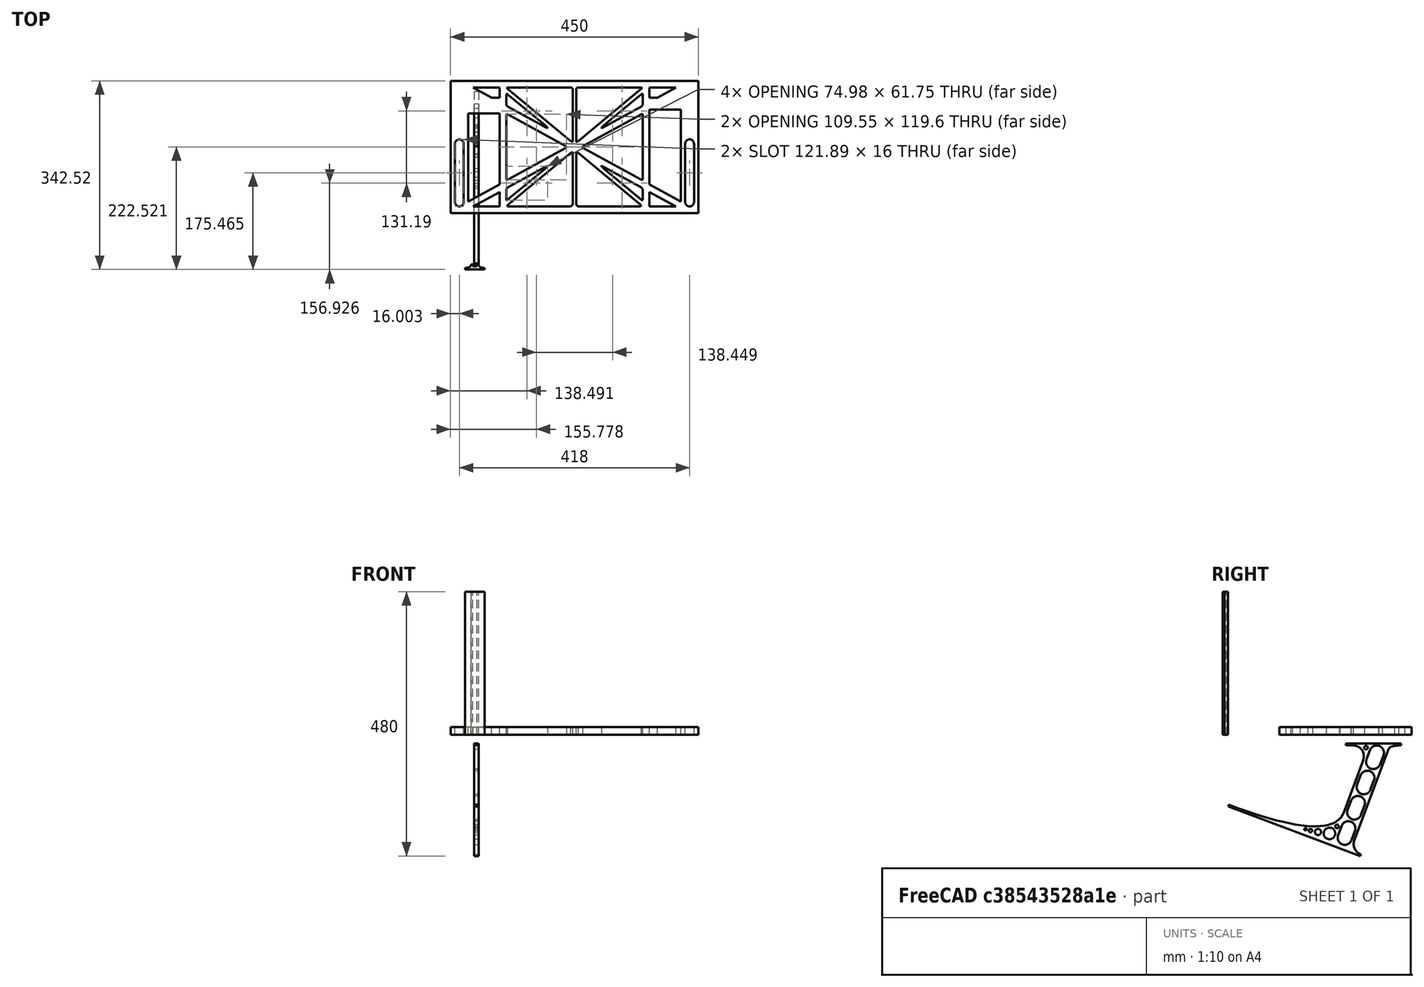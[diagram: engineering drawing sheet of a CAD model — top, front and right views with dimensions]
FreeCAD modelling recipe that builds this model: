
FCSTD DOCUMENT  (FreeCAD 0.19R0.19.2)
Label: laptopStand095
License: All rights reserved
LicenseURL: http://en.wikipedia.org/wiki/All_rights_reserved
objects: Sketcher::SketchObject×3, Part::Extrusion×3
note: 6 computed .brp shape members not serialized (recipe doc carries the construction recipe); baked Part::Feature solids carry a one-line shape summary decoded from their .brp

FEATURE [Sketcher::SketchObject] Sketch
  FullyConstrained = false
  sketch-geometry (252):
    g0: LineSegment StartX=-10.9272 StartY=-82.7794 StartZ=0 EndX=46.0728 EndY=-51.4823 EndZ=0
    g1: LineSegment StartX=366.073 StartY=-91.7794 StartZ=0 EndX=318.073 EndY=-65.424 EndZ=0
    g2: LineSegment StartX=-10.9272 StartY=77.3346 StartZ=0 EndX=-10.9272 EndY=-82.7794 EndZ=0
    g3: LineSegment StartX=375.073 StartY=-82.7794 StartZ=0 EndX=375.073 EndY=83.9235 EndZ=0
    g4: LineSegment StartX=-1.92719 StartY=-91.7794 StartZ=0 EndX=46.0728 EndY=-91.7794 EndZ=0
    g5: LineSegment StartX=318.073 StartY=124.221 StartZ=0 EndX=366.073 EndY=124.221 EndZ=0
    g6: LineSegment StartX=318.073 StartY=83.9235 StartZ=0 EndX=318.073 EndY=-51.4823 EndZ=0
    g7: LineSegment StartX=318.073 StartY=-51.4823 StartZ=0 EndX=375.073 EndY=-82.7794 EndZ=0
    g8: LineSegment StartX=318.073 StartY=-65.424 StartZ=0 EndX=318.073 EndY=-91.7794 EndZ=0
    g9: LineSegment StartX=318.073 StartY=-91.7794 StartZ=0 EndX=366.073 EndY=-91.7794 EndZ=0
    g10: LineSegment StartX=46.0728 StartY=-65.424 StartZ=0 EndX=-1.92719 EndY=-91.7794 EndZ=0
    g11: LineSegment StartX=46.0728 StartY=-65.424 StartZ=0 EndX=46.0728 EndY=-91.7794 EndZ=0
    g12: LineSegment StartX=46.0728 StartY=77.3346 StartZ=0 EndX=46.0728 EndY=-51.4823 EndZ=0
    g13: LineSegment StartX=-42.9272 StartY=136.221 StartZ=0 EndX=-42.9272 EndY=-103.779 EndZ=0
    g14: LineSegment StartX=407.073 StartY=136.221 StartZ=0 EndX=407.073 EndY=-103.779 EndZ=0
    g15: ArcOfCircle CenterX=-26.9272 CenterY=22.1087 CenterZ=0 NormalX=0 NormalY=0 NormalZ=1 AngleXU=0 Radius=8 StartAngle=1e-16 EndAngle=3.14159
    g16: ArcOfCircle CenterX=-26.9272 CenterY=-83.7794 CenterZ=0 NormalX=0 NormalY=0 NormalZ=1 AngleXU=0 Radius=8 StartAngle=3.14159 EndAngle=6.28319
    g17: LineSegment StartX=-34.9272 StartY=22.1087 StartZ=0 EndX=-34.9272 EndY=-83.7794 EndZ=0
    g18: LineSegment StartX=-18.9272 StartY=22.1087 StartZ=0 EndX=-18.9272 EndY=-83.7794 EndZ=0
    g19: ArcOfCircle CenterX=391.073 CenterY=22.1087 CenterZ=0 NormalX=0 NormalY=0 NormalZ=1 AngleXU=0 Radius=8 StartAngle=-4.4e-15 EndAngle=3.14159
    g20: LineSegment StartX=399.073 StartY=22.1087 StartZ=0 EndX=399.073 EndY=-83.7794 EndZ=0
    g21: LineSegment StartX=383.073 StartY=22.1087 StartZ=0 EndX=383.073 EndY=-83.7794 EndZ=0
    g22: ArcOfCircle CenterX=391.073 CenterY=-83.7794 CenterZ=0 NormalX=0 NormalY=0 NormalZ=1 AngleXU=0 Radius=8 StartAngle=3.14159 EndAngle=6.28319
    g23: Circle CenterX=175.022 CenterY=27.0628 CenterZ=0 NormalX=0 NormalY=0 NormalZ=1 AngleXU=0 Radius=1
    g24: Circle CenterX=179.022 CenterY=24.8665 CenterZ=0 NormalX=0 NormalY=0 NormalZ=1 AngleXU=0 Radius=1
    g25: Circle CenterX=179.022 CenterY=27.0628 CenterZ=0 NormalX=0 NormalY=0 NormalZ=1 AngleXU=0 Radius=1
    g26: BSplineCurve PolesCount=3 KnotsCount=2 Degree=2 IsPeriodic=0
    g27: GeomPoint X=175.022 Y=27.0628 Z=0
    g28: GeomPoint X=179.022 Y=27.0628 Z=0
    g29: Circle CenterX=189.124 CenterY=27.0628 CenterZ=0 NormalX=0 NormalY=0 NormalZ=1 AngleXU=0 Radius=1
    g30: Circle CenterX=185.124 CenterY=24.8665 CenterZ=0 NormalX=0 NormalY=0 NormalZ=1 AngleXU=0 Radius=1
    g31: Circle CenterX=185.124 CenterY=27.0628 CenterZ=0 NormalX=0 NormalY=0 NormalZ=1 AngleXU=0 Radius=1
    g32: BSplineCurve PolesCount=3 KnotsCount=2 Degree=2 IsPeriodic=0
    g33: GeomPoint X=189.124 Y=27.0628 Z=0
    g34: GeomPoint X=185.124 Y=27.0628 Z=0
    g35: Circle CenterX=175.022 CenterY=5.37834 CenterZ=0 NormalX=0 NormalY=0 NormalZ=1 AngleXU=0 Radius=1
    g36: Circle CenterX=179.022 CenterY=7.57463 CenterZ=0 NormalX=0 NormalY=0 NormalZ=1 AngleXU=0 Radius=1
    g37: Circle CenterX=179.022 CenterY=5.34704 CenterZ=0 NormalX=0 NormalY=0 NormalZ=1 AngleXU=0 Radius=1
    g38: BSplineCurve PolesCount=3 KnotsCount=2 Degree=2 IsPeriodic=0
    g39: GeomPoint X=175.022 Y=5.37834 Z=0
    g40: GeomPoint X=179.022 Y=5.34704 Z=0
    g41: Circle CenterX=189.124 CenterY=5.37834 CenterZ=0 NormalX=0 NormalY=0 NormalZ=1 AngleXU=0 Radius=1
    g42: Circle CenterX=185.124 CenterY=7.57463 CenterZ=0 NormalX=0 NormalY=0 NormalZ=1 AngleXU=0 Radius=1
    g43: Circle CenterX=185.124 CenterY=5.34704 CenterZ=0 NormalX=0 NormalY=0 NormalZ=1 AngleXU=0 Radius=1
    g44: BSplineCurve PolesCount=3 KnotsCount=2 Degree=2 IsPeriodic=0
    g45: GeomPoint X=189.124 Y=5.37834 Z=0
    g46: GeomPoint X=185.124 Y=5.34704 Z=0
    g47: Circle CenterX=165.871 CenterY=18.1458 CenterZ=0 NormalX=0 NormalY=0 NormalZ=1 AngleXU=0 Radius=1
    g48: Circle CenterX=169.377 CenterY=16.2206 CenterZ=0 NormalX=0 NormalY=0 NormalZ=1 AngleXU=0 Radius=1
    g49: Circle CenterX=165.871 CenterY=14.2954 CenterZ=0 NormalX=0 NormalY=0 NormalZ=1 AngleXU=0 Radius=1
    g50: BSplineCurve PolesCount=3 KnotsCount=2 Degree=2 IsPeriodic=0
    g51: GeomPoint X=165.871 Y=18.1458 Z=0
    g52: GeomPoint X=165.871 Y=14.2954 Z=0
    g53: Circle CenterX=198.275 CenterY=18.1458 CenterZ=0 NormalX=0 NormalY=0 NormalZ=1 AngleXU=0 Radius=1
    g54: Circle CenterX=194.768 CenterY=16.2206 CenterZ=0 NormalX=0 NormalY=0 NormalZ=1 AngleXU=0 Radius=1
    g55: Circle CenterX=198.275 CenterY=14.2954 CenterZ=0 NormalX=0 NormalY=0 NormalZ=1 AngleXU=0 Radius=1
    g56: BSplineCurve PolesCount=3 KnotsCount=2 Degree=2 IsPeriodic=0
    g57: GeomPoint X=198.275 Y=18.1458 Z=0
    g58: GeomPoint X=198.275 Y=14.2954 Z=0
    g59: LineSegment StartX=407.073 StartY=-103.779 StartZ=0 EndX=-42.9272 EndY=-103.779 EndZ=0
    g60: LineSegment StartX=407.073 StartY=136.221 StartZ=0 EndX=-42.9272 EndY=136.221 EndZ=0
    g61: LineSegment StartX=46.0728 StartY=77.3346 StartZ=0 EndX=-10.9272 EndY=77.3346 EndZ=0
    g62: LineSegment StartX=46.0728 StartY=105.865 StartZ=0 EndX=31.5028 EndY=105.865 EndZ=0
    g63: LineSegment StartX=46.0728 StartY=124.221 StartZ=0 EndX=46.0728 EndY=105.865 EndZ=0
    g64: LineSegment StartX=-1.92719 StartY=124.221 StartZ=0 EndX=31.5028 EndY=105.865 EndZ=0
    g65: LineSegment StartX=46.0728 StartY=124.221 StartZ=0 EndX=-1.92719 EndY=124.221 EndZ=0
    g66: LineSegment StartX=318.073 StartY=83.9235 StartZ=0 EndX=375.073 EndY=83.9235 EndZ=0
    g67: Circle CenterX=125.607 CenterY=54.1951 CenterZ=0 NormalX=0 NormalY=0 NormalZ=1 AngleXU=0 Radius=1
    g68: Circle CenterX=139.632 CenterY=46.4944 CenterZ=0 NormalX=0 NormalY=0 NormalZ=1 AngleXU=0 Radius=1
    g69: Circle CenterX=127.326 CenterY=56.7187 CenterZ=0 NormalX=0 NormalY=0 NormalZ=1 AngleXU=0 Radius=1
    g70: BSplineCurve PolesCount=3 KnotsCount=2 Degree=2 IsPeriodic=0
    g71: GeomPoint X=125.607 Y=54.1951 Z=0
    g72: GeomPoint X=127.326 Y=56.7187 Z=0
    g73: Circle CenterX=236.821 CenterY=56.7187 CenterZ=0 NormalX=0 NormalY=0 NormalZ=1 AngleXU=0 Radius=1
    g74: Circle CenterX=224.513 CenterY=46.4944 CenterZ=0 NormalX=0 NormalY=0 NormalZ=1 AngleXU=0 Radius=1
    g75: Circle CenterX=238.538 CenterY=54.1951 CenterZ=0 NormalX=0 NormalY=0 NormalZ=1 AngleXU=0 Radius=1
    g76: BSplineCurve PolesCount=3 KnotsCount=2 Degree=2 IsPeriodic=0
    g77: GeomPoint X=236.821 Y=56.7187 Z=0
    g78: GeomPoint X=238.538 Y=54.1951 Z=0
    g79: Circle CenterX=238.538 CenterY=-21.7539 CenterZ=0 NormalX=0 NormalY=0 NormalZ=1 AngleXU=0 Radius=1
    g80: Circle CenterX=224.513 CenterY=-14.0532 CenterZ=0 NormalX=0 NormalY=0 NormalZ=1 AngleXU=0 Radius=1
    g81: Circle CenterX=236.821 CenterY=-24.2775 CenterZ=0 NormalX=0 NormalY=0 NormalZ=1 AngleXU=0 Radius=1
    g82: BSplineCurve PolesCount=3 KnotsCount=2 Degree=2 IsPeriodic=0
    g83: GeomPoint X=238.538 Y=-21.7539 Z=0
    g84: GeomPoint X=236.821 Y=-24.2775 Z=0
    g85: Circle CenterX=125.607 CenterY=-21.7539 CenterZ=0 NormalX=0 NormalY=0 NormalZ=1 AngleXU=0 Radius=1
    g86: Circle CenterX=139.632 CenterY=-14.0532 CenterZ=0 NormalX=0 NormalY=0 NormalZ=1 AngleXU=0 Radius=1
    g87: Circle CenterX=127.325 CenterY=-24.2775 CenterZ=0 NormalX=0 NormalY=0 NormalZ=1 AngleXU=0 Radius=1
    g88: BSplineCurve PolesCount=3 KnotsCount=2 Degree=2 IsPeriodic=0
    g89: GeomPoint X=125.607 Y=-21.7539 Z=0
    g90: GeomPoint X=127.325 Y=-24.2775 Z=0
    g91: Circle CenterX=302.996 CenterY=111.695 CenterZ=0 NormalX=0 NormalY=0 NormalZ=1 AngleXU=0 Radius=1
    g92: Circle CenterX=306.073 CenterY=114.251 CenterZ=0 NormalX=0 NormalY=0 NormalZ=1 AngleXU=0 Radius=1
    g93: Circle CenterX=306.073 CenterY=110.251 CenterZ=0 NormalX=0 NormalY=0 NormalZ=1 AngleXU=0 Radius=1
    g94: BSplineCurve PolesCount=3 KnotsCount=2 Degree=2 IsPeriodic=0
    g95: GeomPoint X=302.996 Y=111.695 Z=0
    g96: GeomPoint X=306.073 Y=110.251 Z=0
    g97: Circle CenterX=306.073 CenterY=95.2763 CenterZ=0 NormalX=0 NormalY=0 NormalZ=1 AngleXU=0 Radius=1
    g98: Circle CenterX=306.073 CenterY=91.2763 CenterZ=0 NormalX=0 NormalY=0 NormalZ=1 AngleXU=0 Radius=1
    g99: Circle CenterX=302.567 CenterY=89.3511 CenterZ=0 NormalX=0 NormalY=0 NormalZ=1 AngleXU=0 Radius=1
    g100: BSplineCurve PolesCount=3 KnotsCount=2 Degree=2 IsPeriodic=0
    g101: GeomPoint X=306.073 Y=95.2763 Z=0
    g102: GeomPoint X=302.567 Y=89.3511 Z=0
    g103: LineSegment StartX=306.073 StartY=110.251 StartZ=0 EndX=306.073 EndY=95.2763 EndZ=0
    g104: LineSegment StartX=302.996 StartY=111.695 StartZ=0 EndX=236.821 EndY=56.7187 EndZ=0
    g105: LineSegment StartX=238.538 StartY=54.1951 StartZ=0 EndX=302.567 EndY=89.3511 EndZ=0
    g106: Circle CenterX=61.1496 CenterY=111.695 CenterZ=0 NormalX=0 NormalY=0 NormalZ=1 AngleXU=0 Radius=1
    g107: Circle CenterX=58.0728 CenterY=114.251 CenterZ=0 NormalX=0 NormalY=0 NormalZ=1 AngleXU=0 Radius=1
    g108: Circle CenterX=58.0728 CenterY=110.251 CenterZ=0 NormalX=0 NormalY=0 NormalZ=1 AngleXU=0 Radius=1
    g109: BSplineCurve PolesCount=3 KnotsCount=2 Degree=2 IsPeriodic=0
    g110: GeomPoint X=61.1496 Y=111.695 Z=0
    g111: GeomPoint X=58.0728 Y=110.251 Z=0
    g112: Circle CenterX=61.5791 CenterY=89.3511 CenterZ=0 NormalX=0 NormalY=0 NormalZ=1 AngleXU=0 Radius=1
    g113: Circle CenterX=58.0728 CenterY=91.2763 CenterZ=0 NormalX=0 NormalY=0 NormalZ=1 AngleXU=0 Radius=1
    g114: Circle CenterX=58.0728 CenterY=95.2763 CenterZ=0 NormalX=0 NormalY=0 NormalZ=1 AngleXU=0 Radius=1
    g115: BSplineCurve PolesCount=3 KnotsCount=2 Degree=2 IsPeriodic=0
    g116: GeomPoint X=61.5791 Y=89.3511 Z=0
    g117: GeomPoint X=58.0728 Y=95.2763 Z=0
    g118: LineSegment StartX=58.0728 StartY=110.251 StartZ=0 EndX=58.0728 EndY=95.2763 EndZ=0
    g119: LineSegment StartX=61.1496 StartY=111.695 StartZ=0 EndX=127.326 EndY=56.7187 EndZ=0
    g120: LineSegment StartX=125.607 StartY=54.1951 StartZ=0 EndX=61.5791 EndY=89.3511 EndZ=0
    g121: Circle CenterX=61.5791 CenterY=-56.9099 CenterZ=0 NormalX=0 NormalY=0 NormalZ=1 AngleXU=0 Radius=1
    g122: Circle CenterX=58.0728 CenterY=-58.8351 CenterZ=0 NormalX=0 NormalY=0 NormalZ=1 AngleXU=0 Radius=1
    g123: Circle CenterX=58.0728 CenterY=-62.8351 CenterZ=0 NormalX=0 NormalY=0 NormalZ=1 AngleXU=0 Radius=1
    g124: BSplineCurve PolesCount=3 KnotsCount=2 Degree=2 IsPeriodic=0
    g125: GeomPoint X=61.5791 Y=-56.9099 Z=0
    g126: GeomPoint X=58.0728 Y=-62.8351 Z=0
    g127: Circle CenterX=58.0728 CenterY=-77.8102 CenterZ=0 NormalX=0 NormalY=0 NormalZ=1 AngleXU=0 Radius=1
    g128: Circle CenterX=58.0728 CenterY=-81.8102 CenterZ=0 NormalX=0 NormalY=0 NormalZ=1 AngleXU=0 Radius=1
    g129: Circle CenterX=61.1496 CenterY=-79.2541 CenterZ=0 NormalX=0 NormalY=0 NormalZ=1 AngleXU=0 Radius=1
    g130: BSplineCurve PolesCount=3 KnotsCount=2 Degree=2 IsPeriodic=0
    g131: GeomPoint X=58.0728 Y=-77.8102 Z=0
    g132: GeomPoint X=61.1496 Y=-79.2541 Z=0
    g133: LineSegment StartX=58.0728 StartY=-62.8351 StartZ=0 EndX=58.0728 EndY=-77.8102 EndZ=0
    g134: LineSegment StartX=61.1496 StartY=-79.2541 StartZ=0 EndX=127.325 EndY=-24.2775 EndZ=0
    g135: LineSegment StartX=125.607 StartY=-21.7539 StartZ=0 EndX=61.5791 EndY=-56.9099 EndZ=0
    g136: Circle CenterX=302.567 CenterY=-56.9099 CenterZ=0 NormalX=0 NormalY=0 NormalZ=1 AngleXU=0 Radius=1
    g137: Circle CenterX=306.073 CenterY=-58.8351 CenterZ=0 NormalX=0 NormalY=0 NormalZ=1 AngleXU=0 Radius=1
    g138: Circle CenterX=306.073 CenterY=-62.8351 CenterZ=0 NormalX=0 NormalY=0 NormalZ=1 AngleXU=0 Radius=1
    g139: BSplineCurve PolesCount=3 KnotsCount=2 Degree=2 IsPeriodic=0
    g140: GeomPoint X=302.567 Y=-56.9099 Z=0
    g141: GeomPoint X=306.073 Y=-62.8351 Z=0
    g142: Circle CenterX=302.996 CenterY=-79.2541 CenterZ=0 NormalX=0 NormalY=0 NormalZ=1 AngleXU=0 Radius=1
    g143: Circle CenterX=306.073 CenterY=-81.8102 CenterZ=0 NormalX=0 NormalY=0 NormalZ=1 AngleXU=0 Radius=1
    g144: Circle CenterX=306.073 CenterY=-77.8102 CenterZ=0 NormalX=0 NormalY=0 NormalZ=1 AngleXU=0 Radius=1
    g145: BSplineCurve PolesCount=3 KnotsCount=2 Degree=2 IsPeriodic=0
    g146: GeomPoint X=302.996 Y=-79.2541 Z=0
    g147: GeomPoint X=306.073 Y=-77.8102 Z=0
    g148: LineSegment StartX=306.073 StartY=-62.8351 StartZ=0 EndX=306.073 EndY=-77.8102 EndZ=0
    g149: LineSegment StartX=302.996 StartY=-79.2541 StartZ=0 EndX=236.821 EndY=-24.2775 EndZ=0
    g150: LineSegment StartX=238.538 StartY=-21.7539 StartZ=0 EndX=302.567 EndY=-56.9099 EndZ=0
    g151: Circle CenterX=61.6457 CenterY=-88.8112 CenterZ=0 NormalX=0 NormalY=0 NormalZ=1 AngleXU=0 Radius=1
    g152: Circle CenterX=58.0728 CenterY=-91.7794 CenterZ=0 NormalX=0 NormalY=0 NormalZ=1 AngleXU=0 Radius=1
    g153: Circle CenterX=63.9135 CenterY=-91.7794 CenterZ=0 NormalX=0 NormalY=0 NormalZ=1 AngleXU=0 Radius=1
    g154: BSplineCurve PolesCount=3 KnotsCount=2 Degree=2 IsPeriodic=0
    g155: GeomPoint X=61.6457 Y=-88.8112 Z=0
    g156: GeomPoint X=63.9135 Y=-91.7794 Z=0
    g157: Circle CenterX=179.022 CenterY=-85.8163 CenterZ=0 NormalX=0 NormalY=0 NormalZ=1 AngleXU=0 Radius=1
    g158: Circle CenterX=179.022 CenterY=-91.7794 CenterZ=0 NormalX=0 NormalY=0 NormalZ=1 AngleXU=0 Radius=1
    g159: Circle CenterX=171.895 CenterY=-91.7794 CenterZ=0 NormalX=0 NormalY=0 NormalZ=1 AngleXU=0 Radius=1
    g160: BSplineCurve PolesCount=3 KnotsCount=2 Degree=2 IsPeriodic=0
    g161: GeomPoint X=179.022 Y=-85.8163 Z=0
    g162: GeomPoint X=171.895 Y=-91.7794 Z=0
    g163: Circle CenterX=185.124 CenterY=-86.2028 CenterZ=0 NormalX=0 NormalY=0 NormalZ=1 AngleXU=0 Radius=1
    g164: Circle CenterX=185.124 CenterY=-91.7794 CenterZ=0 NormalX=0 NormalY=0 NormalZ=1 AngleXU=0 Radius=1
    g165: Circle CenterX=191.747 CenterY=-91.7794 CenterZ=0 NormalX=0 NormalY=0 NormalZ=1 AngleXU=0 Radius=1
    g166: BSplineCurve PolesCount=3 KnotsCount=2 Degree=2 IsPeriodic=0
    g167: GeomPoint X=185.124 Y=-86.2028 Z=0
    g168: GeomPoint X=191.747 Y=-91.7794 Z=0
    g169: Circle CenterX=299.888 CenterY=-86.6413 CenterZ=0 NormalX=0 NormalY=0 NormalZ=1 AngleXU=0 Radius=1
    g170: Circle CenterX=306.073 CenterY=-91.7794 CenterZ=0 NormalX=0 NormalY=0 NormalZ=1 AngleXU=0 Radius=1
    g171: Circle CenterX=298.776 CenterY=-91.7794 CenterZ=0 NormalX=0 NormalY=0 NormalZ=1 AngleXU=0 Radius=1
    g172: BSplineCurve PolesCount=3 KnotsCount=2 Degree=2 IsPeriodic=0
    g173: GeomPoint X=299.888 Y=-86.6413 Z=0
    g174: GeomPoint X=298.776 Y=-91.7794 Z=0
    g175: LineSegment StartX=189.124 StartY=5.37834 StartZ=0 EndX=299.888 EndY=-86.6413 EndZ=0
    g176: LineSegment StartX=298.776 StartY=-91.7794 StartZ=0 EndX=191.747 EndY=-91.7794 EndZ=0
    g177: LineSegment StartX=185.124 StartY=-86.2028 StartZ=0 EndX=185.124 EndY=5.34704 EndZ=0
    g178: LineSegment StartX=179.022 StartY=5.34704 StartZ=0 EndX=179.022 EndY=-85.8163 EndZ=0
    g179: LineSegment StartX=171.895 StartY=-91.7794 StartZ=0 EndX=63.9135 EndY=-91.7794 EndZ=0
    g180: LineSegment StartX=61.6457 StartY=-88.8112 StartZ=0 EndX=175.022 EndY=5.37834 EndZ=0
    g181: Circle CenterX=302.073 CenterY=124.221 CenterZ=0 NormalX=0 NormalY=0 NormalZ=1 AngleXU=0 Radius=1
    g182: Circle CenterX=306.073 CenterY=124.221 CenterZ=0 NormalX=0 NormalY=0 NormalZ=1 AngleXU=0 Radius=1
    g183: Circle CenterX=302.996 CenterY=121.665 CenterZ=0 NormalX=0 NormalY=0 NormalZ=1 AngleXU=0 Radius=1
    g184: BSplineCurve PolesCount=3 KnotsCount=2 Degree=2 IsPeriodic=0
    g185: GeomPoint X=302.073 Y=124.221 Z=0
    g186: GeomPoint X=302.996 Y=121.665 Z=0
    g187: Circle CenterX=189.124 CenterY=124.221 CenterZ=0 NormalX=0 NormalY=0 NormalZ=1 AngleXU=0 Radius=1
    g188: Circle CenterX=185.124 CenterY=124.221 CenterZ=0 NormalX=0 NormalY=0 NormalZ=1 AngleXU=0 Radius=1
    g189: Circle CenterX=185.124 CenterY=120.221 CenterZ=0 NormalX=0 NormalY=0 NormalZ=1 AngleXU=0 Radius=1
    g190: BSplineCurve PolesCount=3 KnotsCount=2 Degree=2 IsPeriodic=0
    g191: GeomPoint X=189.124 Y=124.221 Z=0
    g192: GeomPoint X=185.124 Y=120.221 Z=0
    g193: Circle CenterX=175.022 CenterY=124.221 CenterZ=0 NormalX=0 NormalY=0 NormalZ=1 AngleXU=0 Radius=1
    g194: Circle CenterX=179.022 CenterY=124.221 CenterZ=0 NormalX=0 NormalY=0 NormalZ=1 AngleXU=0 Radius=1
    g195: Circle CenterX=179.022 CenterY=120.221 CenterZ=0 NormalX=0 NormalY=0 NormalZ=1 AngleXU=0 Radius=1
    g196: BSplineCurve PolesCount=3 KnotsCount=2 Degree=2 IsPeriodic=0
    g197: GeomPoint X=175.022 Y=124.221 Z=0
    g198: GeomPoint X=179.022 Y=120.221 Z=0
    g199: Circle CenterX=62.0728 CenterY=124.221 CenterZ=0 NormalX=0 NormalY=0 NormalZ=1 AngleXU=0 Radius=1
    g200: Circle CenterX=58.0728 CenterY=124.221 CenterZ=0 NormalX=0 NormalY=0 NormalZ=1 AngleXU=0 Radius=1
    g201: Circle CenterX=61.1496 CenterY=121.665 CenterZ=0 NormalX=0 NormalY=0 NormalZ=1 AngleXU=0 Radius=1
    g202: BSplineCurve PolesCount=3 KnotsCount=2 Degree=2 IsPeriodic=0
    g203: GeomPoint X=62.0728 Y=124.221 Z=0
    g204: GeomPoint X=61.1496 Y=121.665 Z=0
    g205: LineSegment StartX=62.0728 StartY=124.221 StartZ=0 EndX=175.022 EndY=124.221 EndZ=0
    g206: LineSegment StartX=179.022 StartY=120.221 StartZ=0 EndX=179.022 EndY=27.0628 EndZ=0
    g207: LineSegment StartX=185.124 StartY=27.0628 StartZ=0 EndX=185.124 EndY=120.221 EndZ=0
    g208: LineSegment StartX=189.124 StartY=124.221 StartZ=0 EndX=302.073 EndY=124.221 EndZ=0
    g209: LineSegment StartX=302.996 StartY=121.665 StartZ=0 EndX=189.124 EndY=27.0628 EndZ=0
    g210: LineSegment StartX=175.022 StartY=27.0628 StartZ=0 EndX=61.1496 EndY=121.665 EndZ=0
    g211: Circle CenterX=61.5791 CenterY=75.4095 CenterZ=0 NormalX=0 NormalY=0 NormalZ=1 AngleXU=0 Radius=1
    g212: Circle CenterX=58.0728 CenterY=77.3346 CenterZ=0 NormalX=0 NormalY=0 NormalZ=1 AngleXU=0 Radius=1
    g213: Circle CenterX=58.0728 CenterY=73.3346 CenterZ=0 NormalX=0 NormalY=0 NormalZ=1 AngleXU=0 Radius=1
    g214: BSplineCurve PolesCount=3 KnotsCount=2 Degree=2 IsPeriodic=0
    g215: GeomPoint X=61.5791 Y=75.4095 Z=0
    g216: GeomPoint X=58.0728 Y=73.3346 Z=0
    g217: Circle CenterX=58.0728 CenterY=-40.8935 CenterZ=0 NormalX=0 NormalY=0 NormalZ=1 AngleXU=0 Radius=1
    g218: Circle CenterX=58.0728 CenterY=-44.8935 CenterZ=0 NormalX=0 NormalY=0 NormalZ=1 AngleXU=0 Radius=1
    g219: Circle CenterX=61.5791 CenterY=-42.9683 CenterZ=0 NormalX=0 NormalY=0 NormalZ=1 AngleXU=0 Radius=1
    g220: BSplineCurve PolesCount=3 KnotsCount=2 Degree=2 IsPeriodic=0
    g221: GeomPoint X=58.0728 Y=-40.8935 Z=0
    g222: GeomPoint X=61.5791 Y=-42.9683 Z=0
    g223: LineSegment StartX=61.5791 StartY=-42.9683 StartZ=0 EndX=165.871 EndY=14.2954 EndZ=0
    g224: LineSegment StartX=165.871 StartY=18.1458 StartZ=0 EndX=61.5791 EndY=75.4095 EndZ=0
    g225: LineSegment StartX=58.0728 StartY=73.3346 StartZ=0 EndX=58.0728 EndY=-40.8935 EndZ=0
    g226: Circle CenterX=302.567 CenterY=-42.9683 CenterZ=0 NormalX=0 NormalY=0 NormalZ=1 AngleXU=0 Radius=1
    g227: Circle CenterX=306.073 CenterY=-44.8935 CenterZ=0 NormalX=0 NormalY=0 NormalZ=1 AngleXU=0 Radius=1
    g228: Circle CenterX=306.073 CenterY=-40.8935 CenterZ=0 NormalX=0 NormalY=0 NormalZ=1 AngleXU=0 Radius=1
    g229: BSplineCurve PolesCount=3 KnotsCount=2 Degree=2 IsPeriodic=0
    g230: GeomPoint X=302.567 Y=-42.9683 Z=0
    g231: GeomPoint X=306.073 Y=-40.8935 Z=0
    g232: Circle CenterX=306.073 CenterY=73.3346 CenterZ=0 NormalX=0 NormalY=0 NormalZ=1 AngleXU=0 Radius=1
    g233: Circle CenterX=306.073 CenterY=77.3346 CenterZ=0 NormalX=0 NormalY=0 NormalZ=1 AngleXU=0 Radius=1
    g234: Circle CenterX=302.567 CenterY=75.4095 CenterZ=0 NormalX=0 NormalY=0 NormalZ=1 AngleXU=0 Radius=1
    g235: BSplineCurve PolesCount=3 KnotsCount=2 Degree=2 IsPeriodic=0
    g236: GeomPoint X=306.073 Y=73.3346 Z=0
    g237: GeomPoint X=302.567 Y=75.4095 Z=0
    g238: LineSegment StartX=302.567 StartY=-42.9683 StartZ=0 EndX=198.275 EndY=14.2954 EndZ=0
    g239: LineSegment StartX=198.275 StartY=18.1458 StartZ=0 EndX=302.567 EndY=75.4095 EndZ=0
    g240: LineSegment StartX=306.073 StartY=73.3346 StartZ=0 EndX=306.073 EndY=-40.8935 EndZ=0
    g241: LineSegment StartX=318.073 StartY=124.221 StartZ=0 EndX=322.073 EndY=124.221 EndZ=0
    g242: LineSegment StartX=366.073 StartY=124.221 StartZ=0 EndX=362.073 EndY=124.221 EndZ=0
    g243: LineSegment StartX=328.643 StartY=105.865 StartZ=0 EndX=332.643 EndY=105.865 EndZ=0
    g244: LineSegment StartX=335.6 StartY=105.351 StartZ=0 EndX=339.311 EndY=107.624 EndZ=0
    g245: LineSegment StartX=366.554 StartY=122.928 StartZ=0 EndX=363.62 EndY=120.771 EndZ=0
    g246: LineSegment StartX=318.073 StartY=105.865 StartZ=0 EndX=318.073 EndY=109.865 EndZ=0
    g247: LineSegment StartX=318.073 StartY=105.865 StartZ=0 EndX=322.073 EndY=105.865 EndZ=0
    g248: LineSegment StartX=318.073 StartY=124.221 StartZ=0 EndX=318.073 EndY=120.221 EndZ=0
    g249: LineSegment StartX=332.643 StartY=105.865 StartZ=0 EndX=366.073 EndY=124.221 EndZ=0
    g250: LineSegment StartX=322.073 StartY=105.865 StartZ=0 EndX=328.643 EndY=105.865 EndZ=0
    g251: LineSegment StartX=318.073 StartY=120.221 StartZ=0 EndX=318.073 EndY=109.865 EndZ=0
  constraints (431):
    c: Horizontal(g4)
    c: Horizontal(g5)
    c: Coincident(g6,g7)
    c: Coincident(g8,g1)
    c: Tangent(g6,g8)
    c: Coincident(g11,g10)
    c: Coincident(g0,g12)
    c: Block(g7)
    c: Block(g3)
    c: Block(g1)
    c: Block(g8)
    c: Block(g11)
    c: Block(g10)
    c: Block(g0)
    c: Block(g2)
    c: Block(g5)
    c: Block(g9)
    c: Block(g4)
    c: Vertical(g13)
    c: Vertical(g14)
    c: Block(g14)
    c: Block(g13)
    c: Tangent(g15,g18) = 1.5708
    c: Tangent(g15,g17) = -1.5708
    c: Tangent(g17,g16) = -1.5708
    c: Tangent(g18,g16) = 1.5708
    c: Vertical(g17)
    c: Equal(g15,g16)
    c: Block(g18)
    c: Block(g17)
    c: Tangent(g19,g20) = 1.5708
    c: Tangent(g20,g22) = 1.5708
    c: Equal(g19,g22)
    c: Coincident(g21,g19)
    c: Coincident(g21,g22)
    c: Block(g20)
    c: Block(g21)
    c: Weight(g23) = 1
    c: Equal(g23,g24)
    c: Equal(g23,g25)
    c: InternalAlignment(g23,g26)
    c: InternalAlignment(g24,g26)
    c: InternalAlignment(g25,g26)
    c: InternalAlignment(g27,g26)
    c: InternalAlignment(g28,g26)
    c: Weight(g29) = 1
    c: Equal(g29,g30)
    c: Equal(g29,g31)
    c: InternalAlignment(g29,g32)
    c: InternalAlignment(g30,g32)
    c: InternalAlignment(g31,g32)
    c: InternalAlignment(g33,g32)
    c: InternalAlignment(g34,g32)
    c: Block(g32)
    c: Block(g26)
    c: Weight(g35) = 1
    c: Equal(g35,g36)
    c: Equal(g35,g37)
    c: InternalAlignment(g35,g38)
    c: InternalAlignment(g36,g38)
    c: InternalAlignment(g37,g38)
    c: InternalAlignment(g39,g38)
    c: InternalAlignment(g40,g38)
    c: Weight(g41) = 1
    c: Equal(g41,g42)
    c: Equal(g41,g43)
    c: InternalAlignment(g41,g44)
    c: InternalAlignment(g42,g44)
    c: InternalAlignment(g43,g44)
    c: InternalAlignment(g45,g44)
    c: InternalAlignment(g46,g44)
    c: Block(g44)
    c: Block(g38)
    c: Weight(g47) = 1
    c: Equal(g47,g48)
    c: Equal(g47,g49)
    c: InternalAlignment(g47,g50)
    c: InternalAlignment(g48,g50)
    c: InternalAlignment(g49,g50)
    c: InternalAlignment(g51,g50)
    c: InternalAlignment(g52,g50)
    c: Weight(g53) = 1
    c: Equal(g53,g54)
    c: Equal(g53,g55)
    c: InternalAlignment(g53,g56)
    c: InternalAlignment(g54,g56)
    c: InternalAlignment(g55,g56)
    c: InternalAlignment(g57,g56)
    c: InternalAlignment(g58,g56)
    c: Block(g50)
    c: Block(g56)
    c: Coincident(g59,g14)
    c: Coincident(g59,g13)
    c: Horizontal(g59)
    c: Distance(g59) = 450
    c: Coincident(g60,g14)
    c: Coincident(g60,g13)
    c: Horizontal(g60)
    c: Horizontal(g61)
    c: Coincident(g12,g61)
    c: Horizontal(g62)
    c: Vertical(g63)
    c: Block(g63)
    c: Block(g62)
    c: Block(g61)
    c: Distance(g63) = 18.3554
    c: Coincident(g65,g63)
    c: Coincident(g65,g64)
    c: Horizontal(g65)
    c: Block(g65)
    c: Block(g64)
    c: Coincident(g62,g64)
    c: Coincident(g2,g61)
    c: Coincident(g66,g6)
    c: Horizontal(g66)
    c: Block(g66)
    c: Coincident(g3,g66)
    c: Weight(g67) = 1
    c: Equal(g67,g68)
    c: Equal(g67,g69)
    c: InternalAlignment(g67,g70)
    c: InternalAlignment(g68,g70)
    c: InternalAlignment(g69,g70)
    c: InternalAlignment(g71,g70)
    c: InternalAlignment(g72,g70)
    c: Block(g70)
    c: Weight(g73) = 1
    c: Equal(g73,g74)
    c: Equal(g73,g75)
    c: InternalAlignment(g73,g76)
    c: InternalAlignment(g74,g76)
    c: InternalAlignment(g75,g76)
    c: InternalAlignment(g77,g76)
    c: InternalAlignment(g78,g76)
    c: Block(g76)
    c: Weight(g79) = 1
    c: Equal(g79,g80)
    c: Equal(g79,g81)
    c: InternalAlignment(g79,g82)
    c: InternalAlignment(g80,g82)
    c: InternalAlignment(g81,g82)
    c: InternalAlignment(g83,g82)
    c: InternalAlignment(g84,g82)
    c: Block(g82)
    c: Weight(g85) = 1
    c: Equal(g85,g86)
    c: Equal(g85,g87)
    c: InternalAlignment(g85,g88)
    c: InternalAlignment(g86,g88)
    c: InternalAlignment(g87,g88)
    c: InternalAlignment(g89,g88)
    c: InternalAlignment(g90,g88)
    c: Block(g88)
    c: Weight(g91) = 1
    c: Equal(g91,g92)
    c: Equal(g91,g93)
    c: InternalAlignment(g91,g94)
    c: InternalAlignment(g92,g94)
    c: InternalAlignment(g93,g94)
    c: InternalAlignment(g95,g94)
    c: InternalAlignment(g96,g94)
    c: Weight(g97) = 1
    c: Equal(g97,g98)
    c: Equal(g97,g99)
    c: InternalAlignment(g97,g100)
    c: InternalAlignment(g98,g100)
    c: InternalAlignment(g99,g100)
    c: InternalAlignment(g101,g100)
    c: InternalAlignment(g102,g100)
    c: Block(g94)
    c: Block(g100)
    c: Coincident(g103,g94)
    c: Coincident(g103,g100)
    c: Vertical(g103)
    c: Coincident(g104,g94)
    c: Coincident(g104,g76)
    c: Coincident(g105,g76)
    c: Coincident(g105,g100)
    c: Weight(g106) = 1
    c: Equal(g106,g107)
    c: Equal(g106,g108)
    c: InternalAlignment(g106,g109)
    c: InternalAlignment(g107,g109)
    c: InternalAlignment(g108,g109)
    c: InternalAlignment(g110,g109)
    c: InternalAlignment(g111,g109)
    c: Weight(g112) = 1
    c: Equal(g112,g113)
    c: Equal(g112,g114)
    c: InternalAlignment(g112,g115)
    c: InternalAlignment(g113,g115)
    c: InternalAlignment(g114,g115)
    c: InternalAlignment(g116,g115)
    c: InternalAlignment(g117,g115)
    c: Block(g109)
    c: Block(g115)
    c: Coincident(g118,g109)
    c: Coincident(g118,g115)
    c: Vertical(g118)
    c: Coincident(g119,g109)
    c: Coincident(g119,g70)
    c: Coincident(g120,g70)
    c: Coincident(g120,g115)
    c: Weight(g121) = 1
    c: Equal(g121,g122)
    c: Equal(g121,g123)
    c: InternalAlignment(g121,g124)
    c: InternalAlignment(g122,g124)
    c: InternalAlignment(g123,g124)
    c: InternalAlignment(g125,g124)
    c: InternalAlignment(g126,g124)
    c: Weight(g127) = 1
    c: Equal(g127,g128)
    c: Equal(g127,g129)
    c: InternalAlignment(g127,g130)
    c: InternalAlignment(g128,g130)
    c: InternalAlignment(g129,g130)
    c: InternalAlignment(g131,g130)
    c: InternalAlignment(g132,g130)
    c: Block(g124)
    c: Block(g130)
    c: Coincident(g133,g124)
    c: Coincident(g133,g130)
    c: Vertical(g133)
    c: Coincident(g134,g130)
    c: Coincident(g134,g88)
    c: Coincident(g135,g88)
    c: Coincident(g135,g124)
    c: Weight(g136) = 1
    c: Equal(g136,g137)
    c: Equal(g136,g138)
    c: InternalAlignment(g136,g139)
    c: InternalAlignment(g137,g139)
    c: InternalAlignment(g138,g139)
    c: InternalAlignment(g140,g139)
    c: InternalAlignment(g141,g139)
    c: Weight(g142) = 1
    c: Equal(g142,g143)
    c: Equal(g142,g144)
    c: InternalAlignment(g142,g145)
    c: InternalAlignment(g143,g145)
    c: InternalAlignment(g144,g145)
    c: InternalAlignment(g146,g145)
    c: InternalAlignment(g147,g145)
    c: Block(g139)
    c: Block(g145)
    c: Coincident(g148,g139)
    c: Coincident(g148,g145)
    c: Vertical(g148)
    c: Coincident(g149,g145)
    c: Coincident(g149,g82)
    c: Coincident(g150,g82)
    c: Coincident(g150,g139)
    c: Weight(g151) = 1
    c: Equal(g151,g152)
    c: Equal(g151,g153)
    c: InternalAlignment(g151,g154)
    c: InternalAlignment(g152,g154)
    c: InternalAlignment(g153,g154)
    c: InternalAlignment(g155,g154)
    c: InternalAlignment(g156,g154)
    c: Weight(g157) = 1
    c: Equal(g157,g158)
    c: Equal(g157,g159)
    c: InternalAlignment(g157,g160)
    c: InternalAlignment(g158,g160)
    c: InternalAlignment(g159,g160)
    c: InternalAlignment(g161,g160)
    c: InternalAlignment(g162,g160)
    c: Weight(g163) = 1
    c: Equal(g163,g164)
    c: Equal(g163,g165)
    c: InternalAlignment(g163,g166)
    c: InternalAlignment(g164,g166)
    c: InternalAlignment(g165,g166)
    c: InternalAlignment(g167,g166)
    c: InternalAlignment(g168,g166)
    c: Weight(g169) = 1
    c: Equal(g169,g170)
    c: Equal(g169,g171)
    c: InternalAlignment(g169,g172)
    c: InternalAlignment(g170,g172)
    c: InternalAlignment(g171,g172)
    c: InternalAlignment(g173,g172)
    c: InternalAlignment(g174,g172)
    c: Block(g172)
    c: Block(g166)
    c: Block(g160)
    c: Block(g154)
    c: Coincident(g175,g44)
    c: Coincident(g175,g172)
    c: Coincident(g176,g172)
    c: Coincident(g176,g166)
    c: Horizontal(g176)
    c: Coincident(g177,g166)
    c: Coincident(g177,g44)
    c: Vertical(g177)
    c: Coincident(g178,g38)
    c: Coincident(g178,g160)
    c: Vertical(g178)
    c: Coincident(g179,g160)
    c: Coincident(g179,g154)
    c: Horizontal(g179)
    c: Coincident(g180,g154)
    c: Coincident(g180,g38)
    c: Weight(g181) = 1
    c: Equal(g181,g182)
    c: Equal(g181,g183)
    c: InternalAlignment(g181,g184)
    c: InternalAlignment(g182,g184)
    c: InternalAlignment(g183,g184)
    c: InternalAlignment(g185,g184)
    c: InternalAlignment(g186,g184)
    c: Weight(g187) = 1
    c: Equal(g187,g188)
    c: Equal(g187,g189)
    c: InternalAlignment(g187,g190)
    c: InternalAlignment(g188,g190)
    c: InternalAlignment(g189,g190)
    c: InternalAlignment(g191,g190)
    c: InternalAlignment(g192,g190)
    c: Weight(g193) = 1
    c: Equal(g193,g194)
    c: Equal(g193,g195)
    c: InternalAlignment(g193,g196)
    c: InternalAlignment(g194,g196)
    c: InternalAlignment(g195,g196)
    c: InternalAlignment(g197,g196)
    c: InternalAlignment(g198,g196)
    c: Weight(g199) = 1
    c: Equal(g199,g200)
    c: Equal(g199,g201)
    c: InternalAlignment(g199,g202)
    c: InternalAlignment(g200,g202)
    c: InternalAlignment(g201,g202)
    c: InternalAlignment(g203,g202)
    c: InternalAlignment(g204,g202)
    c: Block(g202)
    c: Block(g196)
    c: Block(g190)
    c: Block(g184)
    c: Coincident(g205,g202)
    c: Coincident(g205,g196)
    c: Horizontal(g205)
    c: Coincident(g206,g196)
    c: Coincident(g206,g26)
    c: Vertical(g206)
    c: Coincident(g207,g32)
    c: Coincident(g207,g190)
    c: Vertical(g207)
    c: Coincident(g208,g190)
    c: Coincident(g208,g184)
    c: Horizontal(g208)
    c: Coincident(g209,g184)
    c: Coincident(g209,g32)
    c: Coincident(g210,g26)
    c: Coincident(g210,g202)
    c: Weight(g211) = 1
    c: Equal(g211,g212)
    c: Equal(g211,g213)
    c: InternalAlignment(g211,g214)
    c: InternalAlignment(g212,g214)
    c: InternalAlignment(g213,g214)
    c: InternalAlignment(g215,g214)
    c: InternalAlignment(g216,g214)
    c: Weight(g217) = 1
    c: Equal(g217,g218)
    c: Equal(g217,g219)
    c: InternalAlignment(g217,g220)
    c: InternalAlignment(g218,g220)
    c: InternalAlignment(g219,g220)
    c: InternalAlignment(g221,g220)
    c: InternalAlignment(g222,g220)
    c: Block(g220)
    c: Block(g214)
    c: Coincident(g223,g220)
    c: Coincident(g223,g50)
    c: Coincident(g224,g50)
    c: Coincident(g224,g214)
    c: Coincident(g225,g214)
    c: Coincident(g225,g220)
    c: Vertical(g225)
    c: Weight(g226) = 1
    c: Equal(g226,g227)
    c: Equal(g226,g228)
    c: InternalAlignment(g226,g229)
    c: InternalAlignment(g227,g229)
    c: InternalAlignment(g228,g229)
    c: InternalAlignment(g230,g229)
    c: InternalAlignment(g231,g229)
    c: Weight(g232) = 1
    c: Equal(g232,g233)
    c: Equal(g232,g234)
    c: InternalAlignment(g232,g235)
    c: InternalAlignment(g233,g235)
    c: InternalAlignment(g234,g235)
    c: InternalAlignment(g236,g235)
    c: InternalAlignment(g237,g235)
    c: Block(g235)
    c: Block(g229)
    c: Coincident(g238,g229)
    c: Coincident(g238,g56)
    c: Coincident(g239,g56)
    c: Coincident(g239,g235)
    c: Coincident(g240,g235)
    c: Coincident(g240,g229)
    c: Vertical(g240)
    c: Horizontal(g241)
    c: Horizontal(g242)
    c: Horizontal(g243)
    c: Vertical(g246)
    c: Horizontal(g247)
    c: Vertical(g248)
    c: Distance(g243) = 4
    c: Distance(g247) = 4
    c: Distance(g246) = 4
    c: Distance(g248) = 4
    c: Distance(g241) = 4
    c: Distance(g242) = 4
    c: Coincident(g241,g5)
    c: Coincident(g248,g5)
    c: Coincident(g5,g242)
    c: Coincident(g249,g5)
    c: Coincident(g250,g247)
    c: Coincident(g250,g243)
    c: Horizontal(g250)
    c: Block(g250)
    c: Coincident(g251,g248)
    c: Coincident(g251,g246)
    c: Vertical(g251)
    c: Block(g251)
FEATURE [Sketcher::SketchObject] Sketch001
  FullyConstrained = true
  MapMode = 4
  Placement = pos=(0,0,0) rot=(0.57735,0.57735,0.57735;2.0944rad)
  Support = -> [Sketch]
  sketch-geometry (46):
    g0: BSplineCurve PolesCount=3 KnotsCount=2 Degree=2 IsPeriodic=0
    g1: ArcOfCircle CenterX=73.1223 CenterY=-32.291 CenterZ=0 NormalX=0 NormalY=0 NormalZ=1 AngleXU=0 Radius=13 StartAngle=5.92268 EndAngle=9.06428
    g2: ArcOfCircle CenterX=66.7816 CenterY=-49.1439 CenterZ=0 NormalX=0 NormalY=0 NormalZ=1 AngleXU=0 Radius=13 StartAngle=2.78068 EndAngle=5.92131
    g3: ArcOfCircle CenterX=55.9263 CenterY=-78.1807 CenterZ=0 NormalX=0 NormalY=0 NormalZ=1 AngleXU=0 Radius=13 StartAngle=5.92268 EndAngle=9.06428
    g4: ArcOfCircle CenterX=49.5884 CenterY=-95.0342 CenterZ=0 NormalX=0 NormalY=0 NormalZ=1 AngleXU=0 Radius=13 StartAngle=2.78068 EndAngle=5.92131
    g5: ArcOfCircle CenterX=38.7206 CenterY=-124.067 CenterZ=0 NormalX=0 NormalY=0 NormalZ=1 AngleXU=0 Radius=13 StartAngle=5.92268 EndAngle=9.06428
    g6: ArcOfCircle CenterX=32.3875 CenterY=-140.92 CenterZ=0 NormalX=0 NormalY=0 NormalZ=1 AngleXU=0 Radius=13 StartAngle=2.78068 EndAngle=5.92131
    g7: ArcOfCircle CenterX=21.4715 CenterY=-169.934 CenterZ=0 NormalX=0 NormalY=0 NormalZ=1 AngleXU=0 Radius=13 StartAngle=5.92268 EndAngle=9.06428
    g8: ArcOfCircle CenterX=15.1336 CenterY=-186.787 CenterZ=0 NormalX=0 NormalY=0 NormalZ=1 AngleXU=0 Radius=13 StartAngle=2.78068 EndAngle=5.92131
    g9-g12: Circle x4 (B-spline internal-alignment scaffolding for g13; pole/knot coordinates omitted)
    g13: BSplineCurve PolesCount=4 KnotsCount=2 Degree=3 IsPeriodic=0
    g14: GeomPoint X=28.8094 Y=-19.0875 Z=0
    g15: GeomPoint X=47.0443 Y=-50.4712 Z=0
    g16: Circle CenterX=53.5586 CenterY=-23.2695 CenterZ=0 NormalX=0 NormalY=0 NormalZ=1 AngleXU=0 Radius=3.24518
    g17: Circle CenterX=-195.441 CenterY=-127.082 CenterZ=0 NormalX=0 NormalY=0 NormalZ=1 AngleXU=0 Radius=1
    g18: Circle CenterX=-8.24091 CenterY=-197.481 CenterZ=0 NormalX=0 NormalY=0 NormalZ=1 AngleXU=0 Radius=1
    g19: Circle CenterX=12.8789 CenterY=-141.321 CenterZ=0 NormalX=0 NormalY=0 NormalZ=1 AngleXU=0 Radius=1
    g20: BSplineCurve PolesCount=3 KnotsCount=2 Degree=2 IsPeriodic=0
    g21: GeomPoint X=-195.441 Y=-127.082 Z=0
    g22: GeomPoint X=12.8789 Y=-141.321 Z=0
    g23: Circle CenterX=-12.8016 CenterY=-179.036 CenterZ=0 NormalX=0 NormalY=0 NormalZ=1 AngleXU=0 Radius=10.5072
    g24: Circle CenterX=0.933922 CenterY=-166.43 CenterZ=0 NormalX=0 NormalY=0 NormalZ=1 AngleXU=0 Radius=3.26661
    g25: Circle CenterX=-33.5518 CenterY=-176.44 CenterZ=0 NormalX=0 NormalY=0 NormalZ=1 AngleXU=0 Radius=5.64388
    g26: Circle CenterX=-47.2366 CenterY=-173.859 CenterZ=0 NormalX=0 NormalY=0 NormalZ=1 AngleXU=0 Radius=3.01653
    g27: Circle CenterX=-56.2595 CenterY=-171.456 CenterZ=0 NormalX=0 NormalY=0 NormalZ=1 AngleXU=0 Radius=2.12826
    g28: ArcOfCircle CenterX=51.2151 CenterY=-198.473 CenterZ=0 NormalX=0 NormalY=0 NormalZ=1 AngleXU=0 Radius=20 StartAngle=2.78189 EndAngle=4.35269
    g29: LineSegment StartX=32.4951 StartY=-191.433 StartZ=0 EndX=94.6578 EndY=-26.1352 EndZ=0
    g30: LineSegment StartX=43.1192 StartY=-220.001 StartZ=0 EndX=-196.497 EndY=-129.89 EndZ=0
    g31: LineSegment StartX=43.1192 StartY=-220.001 StartZ=0 EndX=44.1752 EndY=-217.193 EndZ=0
    g32: LineSegment StartX=117.223 StartY=-19.0875 StartZ=0 EndX=117.223 EndY=-16.0875 EndZ=0
    g33: LineSegment StartX=117.223 StartY=-16.0875 StartZ=0 EndX=17.2232 EndY=-16.0875 EndZ=0
    g34: LineSegment StartX=17.2232 StartY=-16.0875 StartZ=0 EndX=17.2232 EndY=-19.0875 EndZ=0
    g35: LineSegment StartX=28.8094 StartY=-19.0875 StartZ=0 EndX=17.2232 EndY=-19.0875 EndZ=0
    g36: LineSegment StartX=47.0443 StartY=-50.4712 StartZ=0 EndX=12.8789 EndY=-141.321 EndZ=0
    g37: LineSegment StartX=-195.441 StartY=-127.082 StartZ=0 EndX=-196.497 EndY=-129.89 EndZ=0
    g38: LineSegment StartX=85.2866 StartY=-36.8766 StartZ=0 EndX=78.9396 EndY=-53.7463 EndZ=0
    g39: LineSegment StartX=60.9579 StartY=-27.7053 StartZ=0 EndX=54.6191 EndY=-44.5532 EndZ=0
    g40: LineSegment StartX=68.0907 StartY=-82.7664 StartZ=0 EndX=61.7465 EndY=-99.6365 EndZ=0
    g41: LineSegment StartX=43.7619 StartY=-73.595 StartZ=0 EndX=37.426 EndY=-90.4435 EndZ=0
    g42: LineSegment StartX=50.885 StartY=-128.652 StartZ=0 EndX=44.5456 EndY=-145.522 EndZ=0
    g43: LineSegment StartX=26.5562 StartY=-119.481 StartZ=0 EndX=20.2251 EndY=-136.329 EndZ=0
    g44: LineSegment StartX=9.3071 StartY=-165.349 StartZ=0 EndX=2.97115 EndY=-182.197 EndZ=0
    g45: LineSegment StartX=33.6358 StartY=-174.52 StartZ=0 EndX=27.2917 EndY=-191.39 EndZ=0
  constraints (71):
    c: Block(g0)
    c: Block(g1)
    c: Block(g2)
    c: Block(g4)
    c: Block(g3)
    c: Block(g6)
    c: Block(g5)
    c: Block(g8)
    c: Block(g7)
    c: Weight(g9) = 1
    c: Equal(g9,g10)
    c: Equal(g9,g11)
    c: Equal(g9,g12)
    c: InternalAlignment(g9-g12 -> g13) x4
    c: InternalAlignment(g14,g13)
    c: InternalAlignment(g15,g13)
    c: Block(g16)
    c: Weight(g17) = 1
    c: Equal(g17,g18)
    c: Equal(g17,g19)
    c: InternalAlignment(g17,g20)
    c: InternalAlignment(g18,g20)
    c: InternalAlignment(g19,g20)
    c: InternalAlignment(g21,g20)
    c: InternalAlignment(g22,g20)
    c: Block(g20)
    c: Block(g23)
    c: Block(g24)
    c: Block(g25)
    c: Block(g26)
    c: Block(g27)
    c: Block(g28)
    c: Coincident(g29,g28)
    c: Coincident(g29,g0)
    c: Block(g13)
    c: Coincident(g31,g30)
    c: Coincident(g31,g28)
    c: Block(g31)
    c: Coincident(g32,g0)
    c: Vertical(g32)
    c: Coincident(g33,g32)
    c: Horizontal(g33)
    c: Coincident(g34,g33)
    c: Vertical(g34)
    c: Block(g33)
    c: Coincident(g35,g13)
    c: Coincident(g35,g34)
    c: Horizontal(g35)
    c: Coincident(g36,g13)
    c: Coincident(g36,g20)
    c: Coincident(g37,g20)
    c: Coincident(g37,g30)
    c: Block(g30)
    c: Coincident(g38,g1)
    c: Coincident(g38,g2)
    c: Coincident(g39,g1)
    c: Coincident(g39,g2)
    c: Coincident(g40,g3)
    c: Coincident(g40,g4)
    c: Coincident(g41,g3)
    c: Coincident(g41,g4)
    c: Coincident(g42,g5)
    c: Coincident(g42,g6)
    c: Coincident(g43,g5)
    c: Coincident(g43,g6)
    c: Coincident(g44,g7)
    c: Coincident(g44,g8)
    c: Coincident(g45,g7)
    c: Coincident(g45,g8)
    c: Distance(g30) = 256
    c: Distance(g33) = 100
FEATURE [Part::Extrusion] Extrude002
  Base = -> Sketch001
  Dir = (1,0,0)
  DirMode = 2
  FaceMakerClass = Part::FaceMakerBullseye
  LengthFwd = 8
  LengthRev = 0
  Solid = true
  Symmetric = false
FEATURE [Sketcher::SketchObject] Sketch002
  FullyConstrained = true
  sketch-geometry (20):
    g0: LineSegment StartX=-2.77179 StartY=-200.304 StartZ=0 EndX=5.22821 EndY=-200.304 EndZ=0
    g1: LineSegment StartX=5.22821 StartY=-200.304 StartZ=0 EndX=5.22821 EndY=-197.304 EndZ=0
    g2: LineSegment StartX=-2.77179 StartY=-200.304 StartZ=0 EndX=-2.77179 EndY=-197.304 EndZ=0
    g3: LineSegment StartX=5.22821 StartY=-197.304 StartZ=0 EndX=8.22821 EndY=-197.304 EndZ=0
    g4: LineSegment StartX=-2.77179 StartY=-197.304 StartZ=0 EndX=-5.77179 EndY=-197.304 EndZ=0
    g5: LineSegment StartX=19.2282 StartY=-203.304 StartZ=0 EndX=19.2282 EndY=-206.304 EndZ=0
    g6: LineSegment StartX=-16.7718 StartY=-203.304 StartZ=0 EndX=-16.7718 EndY=-206.304 EndZ=0
    g7: LineSegment StartX=-16.7718 StartY=-206.304 StartZ=0 EndX=19.2282 EndY=-206.304 EndZ=0
    g8: Circle CenterX=-16.7718 CenterY=-203.304 CenterZ=0 NormalX=0 NormalY=0 NormalZ=1 AngleXU=0 Radius=1
    g9: Circle CenterX=-5.77179 CenterY=-203.304 CenterZ=0 NormalX=0 NormalY=0 NormalZ=1 AngleXU=0 Radius=1
    g10: Circle CenterX=-5.77179 CenterY=-197.304 CenterZ=0 NormalX=0 NormalY=0 NormalZ=1 AngleXU=0 Radius=1
    g11: BSplineCurve PolesCount=3 KnotsCount=2 Degree=2 IsPeriodic=0
    g12: GeomPoint X=-16.7718 Y=-203.304 Z=0
    g13: GeomPoint X=-5.77179 Y=-197.304 Z=0
    g14: Circle CenterX=19.2282 CenterY=-203.304 CenterZ=0 NormalX=0 NormalY=0 NormalZ=1 AngleXU=0 Radius=1
    g15: Circle CenterX=8.22821 CenterY=-203.304 CenterZ=0 NormalX=0 NormalY=0 NormalZ=1 AngleXU=0 Radius=1
    g16: Circle CenterX=8.22821 CenterY=-197.304 CenterZ=0 NormalX=0 NormalY=0 NormalZ=1 AngleXU=0 Radius=1
    g17: BSplineCurve PolesCount=3 KnotsCount=2 Degree=2 IsPeriodic=0
    g18: GeomPoint X=19.2282 Y=-203.304 Z=0
    g19: GeomPoint X=8.22821 Y=-197.304 Z=0
  constraints (41):
    c: Horizontal(g0)
    c: Distance(g0) = 8
    c: Coincident(g1,g0)
    c: Vertical(g1)
    c: Distance(g1) = 3
    c: Coincident(g2,g0)
    c: Vertical(g2)
    c: Distance(g2) = 3
    c: Coincident(g3,g1)
    c: Horizontal(g3)
    c: Distance(g3) = 3
    c: Coincident(g4,g2)
    c: Horizontal(g4)
    c: Distance(g4) = 3
    c: Vertical(g5)
    c: Vertical(g6)
    c: Coincident(g7,g6)
    c: Coincident(g7,g5)
    c: Weight(g8) = 1
    c: Equal(g8,g9)
    c: Equal(g8,g10)
    c: Coincident(g11,g4)
    c: InternalAlignment(g8,g11)
    c: InternalAlignment(g9,g11)
    c: InternalAlignment(g10,g11)
    c: InternalAlignment(g12,g11)
    c: InternalAlignment(g13,g11)
    c: Coincident(g17,g5)
    c: Weight(g14) = 1
    c: Equal(g14,g15)
    c: Equal(g14,g16)
    c: Coincident(g17,g3)
    c: InternalAlignment(g14,g17)
    c: InternalAlignment(g15,g17)
    c: InternalAlignment(g16,g17)
    c: InternalAlignment(g18,g17)
    c: InternalAlignment(g19,g17)
    c: Block(g7)
    c: Block(g17)
    c: Block(g11)
    c: Block(g6)
FEATURE [Part::Extrusion] Extrude003
  Base = -> Sketch002
  Dir = (0,0,1)
  DirMode = 2
  FaceMakerClass = Part::FaceMakerBullseye
  LengthFwd = 260
  LengthRev = 0
  Solid = true
  Symmetric = false
FEATURE [Part::Extrusion] Extrude
  Base = -> Sketch
  Dir = (0,0,1)
  DirMode = 2
  FaceMakerClass = Part::FaceMakerBullseye
  LengthFwd = 14
  LengthRev = 0
  Solid = true
  Symmetric = false
